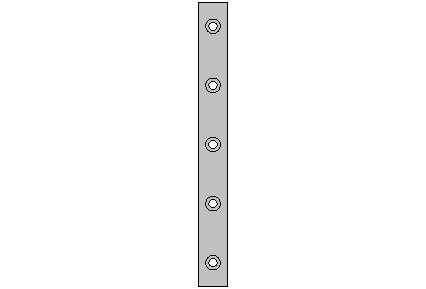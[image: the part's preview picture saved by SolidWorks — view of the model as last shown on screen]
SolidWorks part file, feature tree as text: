
SOLIDWORKS PART (.sldprt)
format: sldprt  version: not decoded by parser v0  size: 135,168 bytes
history: native  units: mm
features: sketch x3, extrude x1, hole x1 (+10 scaffold rows collapsed)
feature tree (15):
  scaffold x10  (default folders/planes/origin — collapsed)
  sketch  "Sketch1"  dims[D1=12.0mm D2=9.0mm]
  extrude  "Extrude1"  Depth=120mm
  hole  "CBORE for M3 SHCS1"  Diameter=3.5mm Depth=9mm
  sketch  "Sketch3"  dims[D1=10.0mm D2=25.0mm D3=25.0mm D4=25.0mm D5=10.0mm]
  sketch  "Sketch2"  dims[hole-wizard template sketch: 41 standard entries collapsed; hole parameters kept: c12.Thru Hole Dia.=3.5mm c12.Thru Hole Depth=9.0mm c12.C'Bore Dia.=6.2mm c12.C'Bore Depth=6.0mm]
decode coverage: 5 of 5 modeling features carry decoded parameters
note: ~ marks probable driven/reference dimensions
note: suppression state not decoded; provenance and decode notes live in map.json
